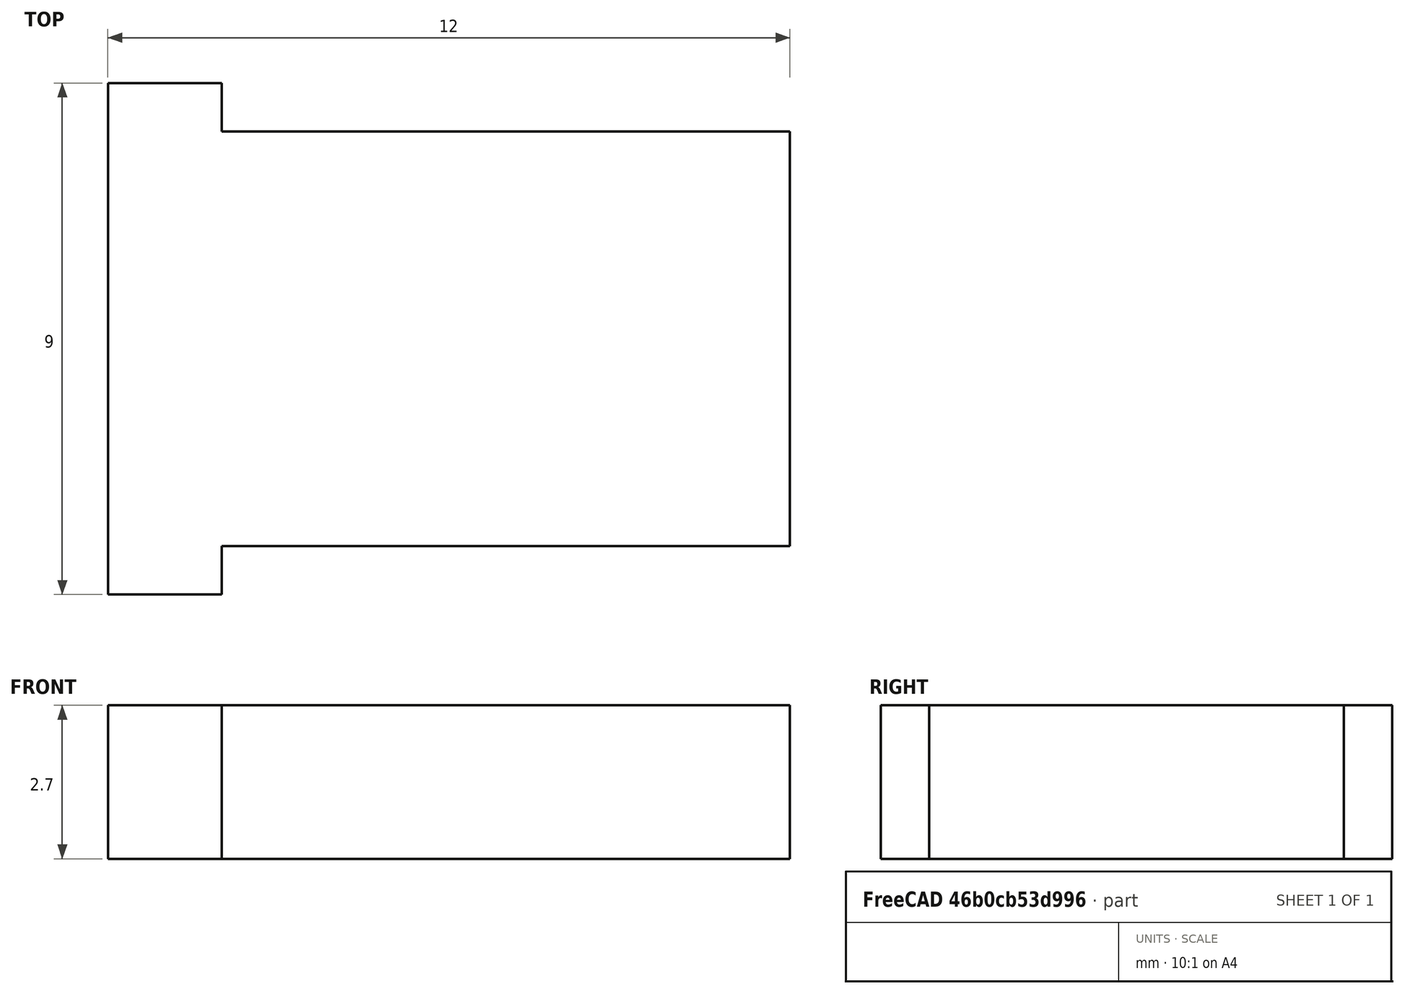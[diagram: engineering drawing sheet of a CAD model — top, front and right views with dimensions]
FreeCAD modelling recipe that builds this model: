
FCSTD DOCUMENT  (FreeCAD 0.16R6707 (Git))
Label: BlocAxe
License: All rights reserved
LicenseURL: http://en.wikipedia.org/wiki/All_rights_reserved
objects: Sketcher::SketchObject×1, PartDesign::Pad×1
note: 3 computed .brp shape members not serialized (recipe doc carries the construction recipe); baked Part::Feature solids carry a one-line shape summary decoded from their .brp

FEATURE [Sketcher::SketchObject] Sketch
  sketch-geometry (9):
    g0: LineSegment StartX=-4.3273 StartY=3.65 StartZ=0 EndX=5.6727 EndY=3.65 EndZ=0
    g1: LineSegment StartX=5.6727 StartY=3.65 StartZ=0 EndX=5.6727 EndY=-3.65 EndZ=0
    g2: LineSegment StartX=5.6727 StartY=-3.65 StartZ=0 EndX=-4.3273 EndY=-3.65 EndZ=0
    g3: LineSegment StartX=-4.3273 StartY=-3.65 StartZ=0 EndX=-4.3273 EndY=-4.5 EndZ=0
    g4: LineSegment StartX=-4.3273 StartY=-4.5 StartZ=0 EndX=-6.3273 EndY=-4.5 EndZ=0
    g5: LineSegment StartX=-6.3273 StartY=-4.5 StartZ=0 EndX=-6.3273 EndY=4.5 EndZ=0
    g6: LineSegment StartX=-6.3273 StartY=4.5 StartZ=0 EndX=-4.3273 EndY=4.5 EndZ=0
    g7: LineSegment StartX=-4.3273 StartY=4.5 StartZ=0 EndX=-4.3273 EndY=3.65 EndZ=0
    g8: LineSegment [constr] StartX=-4.3273 StartY=3.65 StartZ=0 EndX=-4.3273 EndY=-3.65 EndZ=0
  constraints (25):
    c: Horizontal(g0)
    c: Coincident(g1,g0)
    c: Horizontal(g4)
    c: Coincident(g5,g4)
    c: Coincident(g6,g5)
    c: Coincident(g6,g7)
    c: Coincident(g0,g7)
    c: Coincident(g2,g3)
    c: Coincident(g3,g4)
    c: Coincident(g1,g2)
    c: Vertical(g1)
    c: Horizontal(g2)
    c: Vertical(g3)
    c: Vertical(g7)
    c: Vertical(g5)
    c: Horizontal(g6)
    c: Vertical(g8)
    c: Coincident(g2,g8)
    c: Coincident(g0,g8)
    c: Symmetric(g0,g2,g-1)
    c: Symmetric(g5,g4,g-1)
    c: DistanceY(g1,g0) = 7.3
    c: DistanceY(g3,g6) = 9
    c: DistanceX(g5,g6) = 2
    c: DistanceX(g0,g0) = 10
FEATURE [PartDesign::Pad] Pad
  Length = 2.7
  Length2 = 100
  Sketch = -> Sketch
  Type = 0
